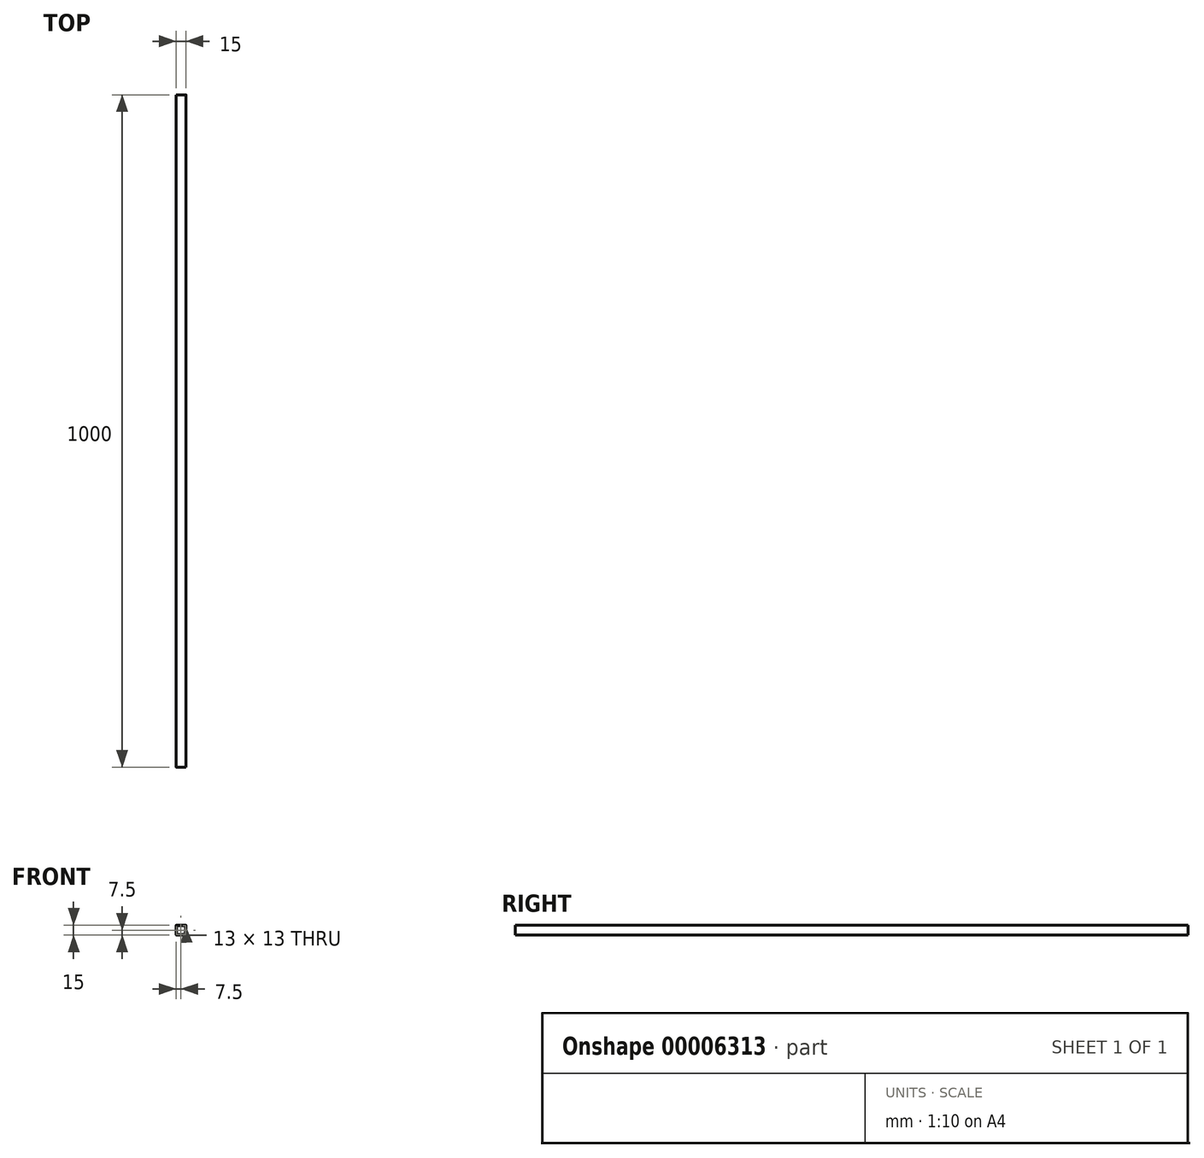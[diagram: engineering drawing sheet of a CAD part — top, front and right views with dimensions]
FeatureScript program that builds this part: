
annotation { "Feature Type Name" : "Feature", "Feature Type Description" : "" }
export const myFeature = defineFeature(function(context is Context, id is Id, definition is map)
    precondition{}
    {
        {
            var Q0;
            Q0=qCreatedBy(makeId("Front.planeOp"),FACE);
            var sketch = newSketch(context, id + "F0", { "sketchPlane" : qUnion([Q0])});
            skLineSegment(sketch, "E0.bottom", {"start": v(0, 0) * mm, "end": v(15, 0) * mm});
            skLineSegment(sketch, "E0.top", {"start": v(0, 15) * mm, "end": v(15, 15) * mm});
            skLineSegment(sketch, "E0.left", {"start": v(0, 0) * mm, "end": v(0, 15) * mm});
            skLineSegment(sketch, "E0.right", {"start": v(15, 0) * mm, "end": v(15, 15) * mm});
            skLineSegment(sketch, "E1.bottom", {"start": v(1, 1) * mm, "end": v(14, 1) * mm});
            skLineSegment(sketch, "E1.top", {"start": v(1, 14) * mm, "end": v(14, 14) * mm});
            skLineSegment(sketch, "E1.left", {"start": v(1, 1) * mm, "end": v(1, 14) * mm});
            skLineSegment(sketch, "E1.right", {"start": v(14, 1) * mm, "end": v(14, 14) * mm});
            skSolve(sketch);
        }
        {
            var Q0;
            Q0=makeQuery(id+"F0.imprint","IMPRINT",FACE,{"disambiguationData":[TD([[makeQuery(id+"F0.imprint","IMPRINT",EDGE,{"derivedFrom":sQuery(id+"F0.wireOp",EDGE,"E0.bottom")}),1.0]])]});
            extrude(context, id + "F1", {"entities" : qUnion([Q0]), "oppositeDirection" : true, "depth" : 1000 * mm});
        }
        {
            var Q0;
            Q0=makeQuery(id+"F1.opExtrude","SWEPT_EDGE",EDGE,{"disambiguationData":[OSD([sQuery(id+"F0.wireOp",EDGE,"E0.top"),sQuery(id+"F0.wireOp",EDGE,"E0.right")])]});
            var Q1;
            Q1=makeQuery(id+"F1.opExtrude","SWEPT_EDGE",EDGE,{"disambiguationData":[OSD([sQuery(id+"F0.wireOp",EDGE,"E0.bottom"),sQuery(id+"F0.wireOp",EDGE,"E0.right")])]});
            var Q2;
            Q2=makeQuery(id+"F1.opExtrude","SWEPT_EDGE",EDGE,{"disambiguationData":[OSD([sQuery(id+"F0.wireOp",EDGE,"E0.top"),sQuery(id+"F0.wireOp",EDGE,"E0.left")])]});
            var Q3;
            Q3=makeQuery(id+"F1.opExtrude","SWEPT_EDGE",EDGE,{"disambiguationData":[OSD([sQuery(id+"F0.wireOp",EDGE,"E0.bottom"),sQuery(id+"F0.wireOp",EDGE,"E0.left")])]});
            fillet(context, id + "F2", {"entities" : qUnion([Q0, Q1, Q2, Q3]), "radius" : .5 * mm, "tangentPropagation" : true, "allowEdgeOverflow" : false});
        }
    });
